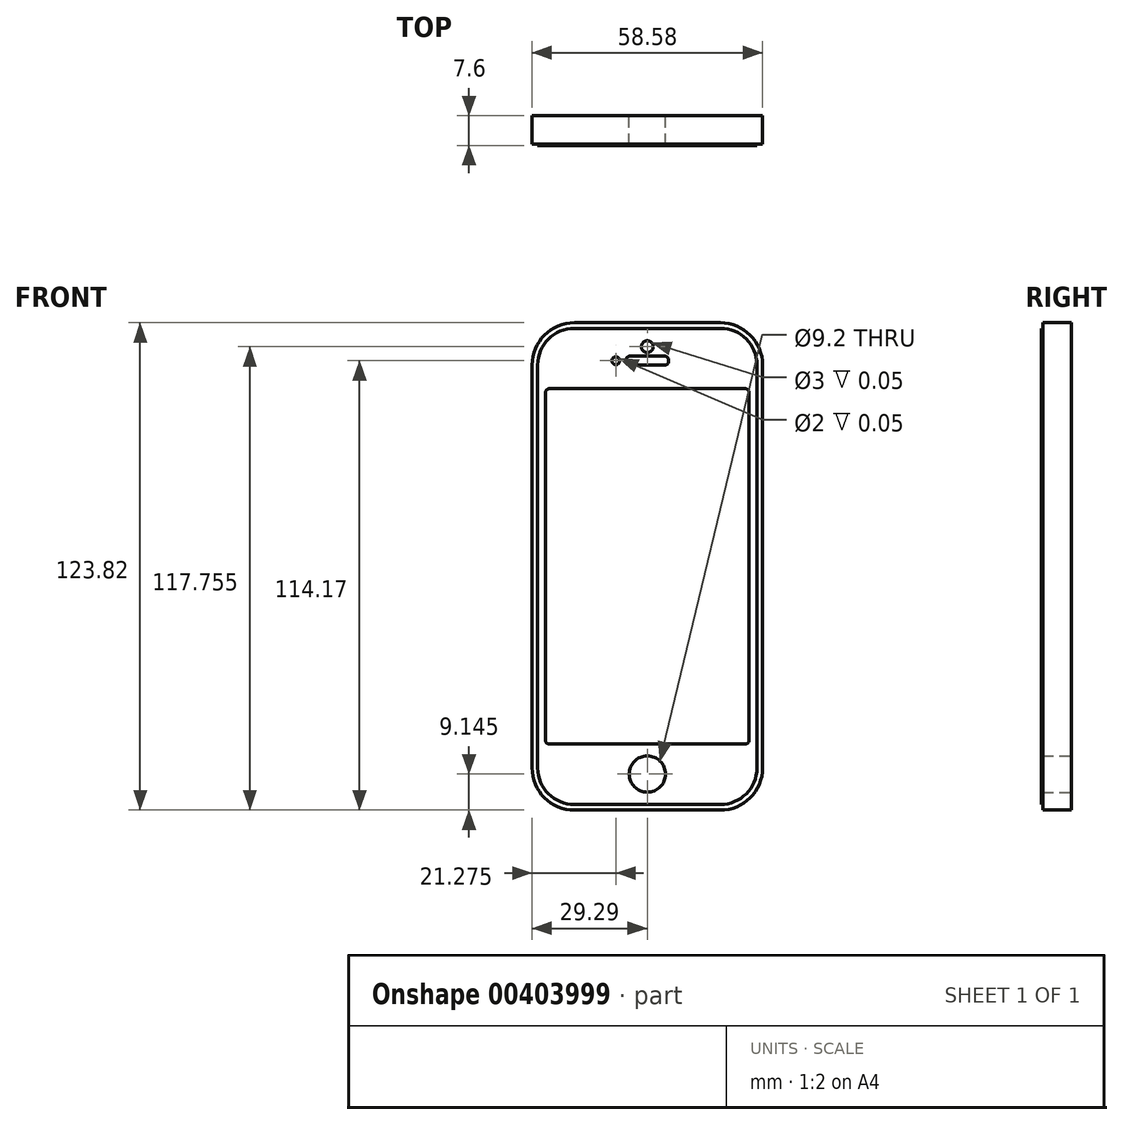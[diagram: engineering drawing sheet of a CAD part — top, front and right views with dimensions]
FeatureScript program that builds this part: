
annotation { "Feature Type Name" : "Feature", "Feature Type Description" : "" }
export const myFeature = defineFeature(function(context is Context, id is Id, definition is map)
    precondition{}
    {
        {
            var Q0;
            Q0=qCreatedBy(makeId("Front.planeOp"),FACE);
            var sketch = newSketch(context, id + "F0", { "sketchPlane" : qUnion([Q0])});
            skLineSegment(sketch, "E0.bottom", {"start": v(18.54, -61.92) * mm, "end": v(-18.53, -61.92) * mm});
            skLineSegment(sketch, "E0.top", {"start": v(18.53, 61.91) * mm, "end": v(-18.54, 61.91) * mm});
            skLineSegment(sketch, "E0.left", {"start": v(29.29, -51.16) * mm, "end": v(29.29, 51.16) * mm});
            skLineSegment(sketch, "E0.right", {"start": v(-29.28, -51.16) * mm, "end": v(-29.29, 51.16) * mm});
            skPoint(sketch, "E0.middle", {"position": v(0, 0) * mm});
            skLineSegment(sketch, "E1.bottom", {"start": v(24.85, -45.15) * mm, "end": v(-24.85, -45.15) * mm});
            skLineSegment(sketch, "E1.top", {"start": v(24.85, 45.15) * mm, "end": v(-24.85, 45.15) * mm});
            skLineSegment(sketch, "E1.left", {"start": v(25.85, -44.15) * mm, "end": v(25.85, 44.15) * mm});
            skLineSegment(sketch, "E1.right", {"start": v(-25.85, -44.15) * mm, "end": v(-25.85, 44.15) * mm});
            skCircle(sketch, "E2", {"center": v(0, -52.77) * mm, "radius": 4.6 * mm});
            skPoint(sketch, "E3.visualSharp", {"position": v(-25.85, 45.15) * mm});
            skArc(sketch, "E3.filletArc", {"start": v(-24.85, 45.15) * mm, "mid": v(-25.56, 44.86) * mm, "end": v(-25.85, 44.15) * mm});
            skPoint(sketch, "E4.visualSharp", {"position": v(25.85, 45.15) * mm});
            skArc(sketch, "E4.filletArc", {"start": v(25.85, 44.15) * mm, "mid": v(25.56, 44.86) * mm, "end": v(24.85, 45.15) * mm});
            skPoint(sketch, "E5.visualSharp", {"position": v(-25.85, -45.15) * mm});
            skArc(sketch, "E5.filletArc", {"start": v(-25.85, -44.15) * mm, "mid": v(-25.56, -44.86) * mm, "end": v(-24.85, -45.15) * mm});
            skPoint(sketch, "E6.visualSharp", {"position": v(25.85, -45.15) * mm});
            skArc(sketch, "E6.filletArc", {"start": v(24.85, -45.15) * mm, "mid": v(25.56, -44.86) * mm, "end": v(25.85, -44.15) * mm});
            skPoint(sketch, "E7.visualSharp", {"position": v(-29.29, 61.92) * mm});
            skArc(sketch, "E7.filletArc", {"start": v(-18.54, 61.91) * mm, "mid": v(-26.14, 58.77) * mm, "end": v(-29.29, 51.16) * mm});
            skPoint(sketch, "E8.visualSharp", {"position": v(29.29, 61.92) * mm});
            skArc(sketch, "E8.filletArc", {"start": v(29.28, 51.16) * mm, "mid": v(26.14, 58.77) * mm, "end": v(18.53, 61.91) * mm});
            skPoint(sketch, "E9.visualSharp", {"position": v(29.29, -61.92) * mm});
            skArc(sketch, "E9.filletArc", {"start": v(18.54, -61.92) * mm, "mid": v(26.14, -58.77) * mm, "end": v(29.29, -51.16) * mm});
            skPoint(sketch, "E10.visualSharp", {"position": v(-29.28, -61.92) * mm});
            skArc(sketch, "E10.filletArc", {"start": v(-29.28, -51.16) * mm, "mid": v(-26.14, -58.77) * mm, "end": v(-18.53, -61.92) * mm});
            skLineSegment(sketch, "E11.bottom", {"start": v(4.4, 53.4) * mm, "end": v(-4.4, 53.4) * mm});
            skLineSegment(sketch, "E11.top", {"start": v(4.4, 51.1) * mm, "end": v(-4.4, 51.1) * mm});
            skLineSegment(sketch, "E11.left", {"start": v(5.4, 52.4) * mm, "end": v(5.4, 52.1) * mm});
            skLineSegment(sketch, "E11.right", {"start": v(-5.4, 52.4) * mm, "end": v(-5.4, 52.1) * mm});
            skPoint(sketch, "E11.middle", {"position": v(0, 52.26) * mm});
            skPoint(sketch, "E12.visualSharp", {"position": v(-5.4, 51.1) * mm});
            skArc(sketch, "E12.filletArc", {"start": v(-5.4, 52.1) * mm, "mid": v(-5.11, 51.4) * mm, "end": v(-4.4, 51.1) * mm});
            skPoint(sketch, "E13.visualSharp", {"position": v(-5.4, 53.4) * mm});
            skArc(sketch, "E13.filletArc", {"start": v(-4.4, 53.4) * mm, "mid": v(-5.11, 53.12) * mm, "end": v(-5.4, 52.4) * mm});
            skPoint(sketch, "E14.visualSharp", {"position": v(5.4, 51.1) * mm});
            skArc(sketch, "E14.filletArc", {"start": v(4.4, 51.1) * mm, "mid": v(5.11, 51.4) * mm, "end": v(5.4, 52.1) * mm});
            skPoint(sketch, "E15.visualSharp", {"position": v(5.4, 53.4) * mm});
            skArc(sketch, "E15.filletArc", {"start": v(5.4, 52.4) * mm, "mid": v(5.11, 53.12) * mm, "end": v(4.4, 53.4) * mm});
            skCircle(sketch, "E16", {"center": v(0, 55.84) * mm, "radius": 1.5 * mm});
            skCircle(sketch, "E17", {"center": v(-8.01, 52.26) * mm, "radius": 1 * mm});
            skLineSegment(sketch, "E18.bottom", {"start": v(18.6, -60.48) * mm, "end": v(-18.6, -60.48) * mm});
            skLineSegment(sketch, "E18.top", {"start": v(18.6, 60.48) * mm, "end": v(-18.6, 60.48) * mm});
            skLineSegment(sketch, "E18.left", {"start": v(27.85, -51.23) * mm, "end": v(27.85, 51.23) * mm});
            skLineSegment(sketch, "E18.right", {"start": v(-27.85, -51.23) * mm, "end": v(-27.85, 51.23) * mm});
            skPoint(sketch, "E19.visualSharp", {"position": v(-27.85, -60.48) * mm});
            skArc(sketch, "E19.filletArc", {"start": v(-27.85, -51.23) * mm, "mid": v(-25.14, -57.77) * mm, "end": v(-18.6, -60.48) * mm});
            skPoint(sketch, "E20.visualSharp", {"position": v(27.85, -60.48) * mm});
            skArc(sketch, "E20.filletArc", {"start": v(18.6, -60.48) * mm, "mid": v(25.14, -57.77) * mm, "end": v(27.85, -51.23) * mm});
            skPoint(sketch, "E21.visualSharp", {"position": v(27.85, 60.48) * mm});
            skArc(sketch, "E21.filletArc", {"start": v(27.85, 51.23) * mm, "mid": v(25.14, 57.77) * mm, "end": v(18.6, 60.48) * mm});
            skPoint(sketch, "E22.visualSharp", {"position": v(-27.85, 60.48) * mm});
            skArc(sketch, "E22.filletArc", {"start": v(-18.6, 60.48) * mm, "mid": v(-25.14, 57.77) * mm, "end": v(-27.85, 51.23) * mm});
            skCircle(sketch, "E23", {"center": v(0, -52.77) * mm, "radius": 4.2 * mm});
            skSolve(sketch);
        }
        {
            var Q0;
            Q0=makeQuery(id+"F0.imprint","IMPRINT",FACE,{"disambiguationData":[TD([[makeQuery(id+"F0.imprint","IMPRINT",EDGE,{"derivedFrom":sQuery(id+"F0.wireOp",EDGE,"E1.bottom")}),1.0]])]});
            extrude(context, id + "F1", {"entities" : qUnion([Q0]), "depth" : 7.6 * mm});
        }
        {
            var Q0;
            Q0=makeQuery(id+"F0.imprint","IMPRINT",FACE,{"disambiguationData":[TD([[makeQuery(id+"F0.imprint","IMPRINT",EDGE,{"derivedFrom":sQuery(id+"F0.wireOp",EDGE,"E0.bottom")}),-1.0]])]});
            extrude(context, id + "F2", {"entities" : qUnion([Q0]), "operationType" : NewBodyOperationType.ADD, "depth" : 7.25 * mm});
        }
        {
            var Q0;
            Q0=makeQuery(id+"F0.imprint","IMPRINT",FACE,{"disambiguationData":[TD([[makeQuery(id+"F0.imprint","IMPRINT",EDGE,{"derivedFrom":sQuery(id+"F0.wireOp",EDGE,"E1.bottom")}),-1.0]])]});
            extrude(context, id + "F3", {"entities" : qUnion([Q0]), "operationType" : NewBodyOperationType.ADD, "depth" : 7.55 * mm});
        }
        {
            var Q0;
            Q0=makeQuery(id+"F0.imprint","IMPRINT",FACE,{"disambiguationData":[TD([[makeQuery(id+"F0.imprint","IMPRINT",EDGE,{"derivedFrom":sQuery(id+"F0.wireOp",EDGE,"E16")}),1.0]])]});
            extrude(context, id + "F4", {"entities" : qUnion([Q0]), "operationType" : NewBodyOperationType.ADD, "depth" : 7.55 * mm});
        }
        {
            var Q0;
            Q0=makeQuery(id+"F0.imprint","IMPRINT",FACE,{"disambiguationData":[TD([[makeQuery(id+"F0.imprint","IMPRINT",EDGE,{"derivedFrom":sQuery(id+"F0.wireOp",EDGE,"E17")}),1.0]])]});
            extrude(context, id + "F5", {"entities" : qUnion([Q0]), "operationType" : NewBodyOperationType.ADD, "depth" : 7.55 * mm});
        }
        {
            var Q0;
            Q0=makeQuery(id+"F0.imprint","IMPRINT",FACE,{"disambiguationData":[TD([[makeQuery(id+"F0.imprint","IMPRINT",EDGE,{"derivedFrom":sQuery(id+"F0.wireOp",EDGE,"E11.bottom")}),1.0]])]});
            extrude(context, id + "F6", {"entities" : qUnion([Q0]), "operationType" : NewBodyOperationType.ADD, "depth" : 7.25 * mm});
        }
        {
            var Q0;
            Q0=makeQuery(id+"F0.imprint","IMPRINT",FACE,{"disambiguationData":[TD([[makeQuery(id+"F0.imprint","IMPRINT",EDGE,{"derivedFrom":sQuery(id+"F0.wireOp",EDGE,"E23")}),1.0]])]});
            extrude(context, id + "F7", {"entities" : qUnion([Q0]), "depth" : 7 * mm});
        }
        {
            var Q0;
            Q0=makeQuery(id+"F7.opExtrude","SWEPT_BODY",BODY,{"disambiguationData":[OSD([sQuery(id+"F0.wireOp",EDGE,"E23")])]});
            deleteBodies(context, id + "F8", {"entities" : qUnion([Q0])});
        }
    });
